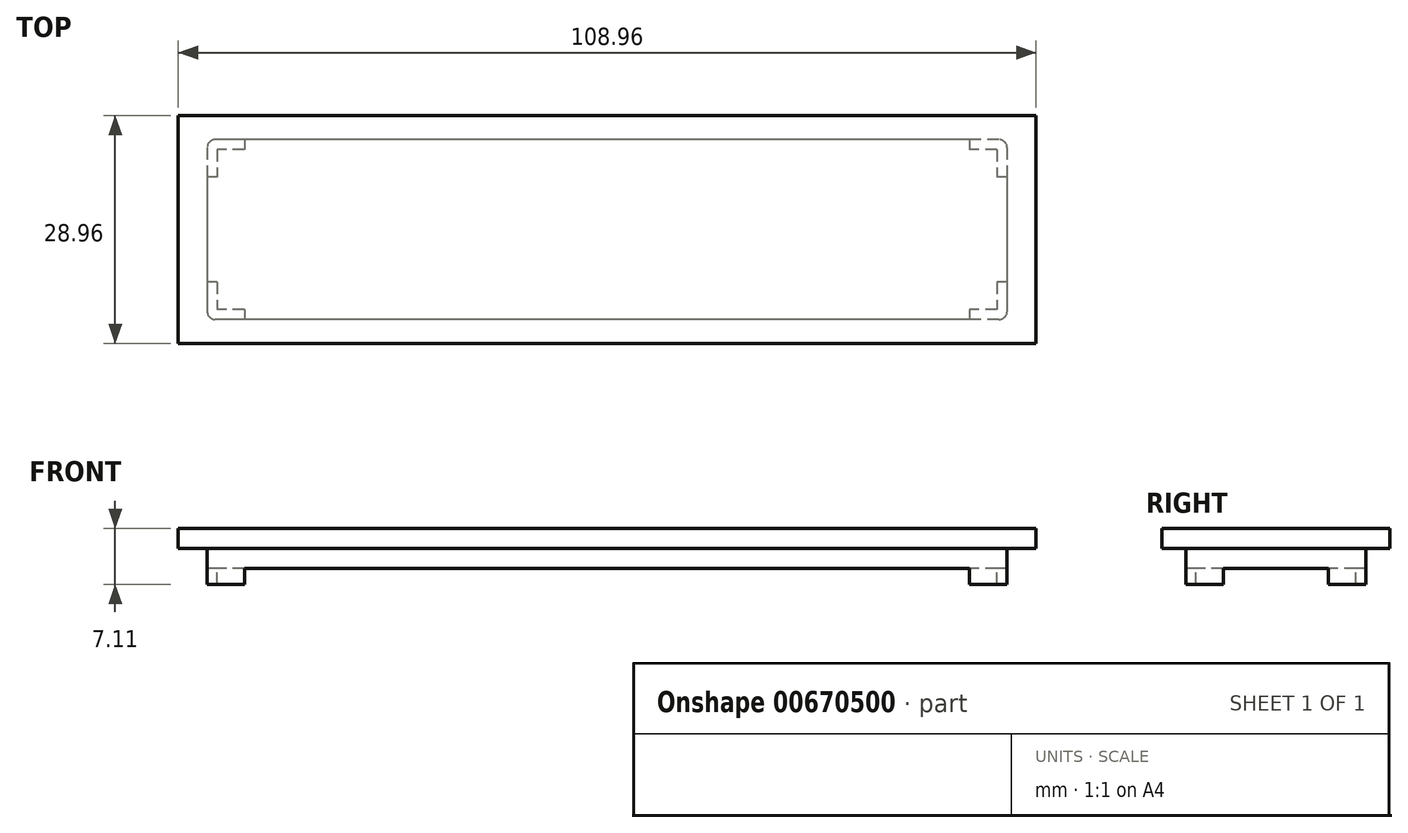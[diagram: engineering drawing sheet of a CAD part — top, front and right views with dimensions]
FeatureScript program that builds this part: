
annotation { "Feature Type Name" : "Feature", "Feature Type Description" : "" }
export const myFeature = defineFeature(function(context is Context, id is Id, definition is map)
    precondition{}
    {
        {
            var Q0;
            Q0=qCreatedBy(makeId("Top.planeOp"),FACE);
            var sketch = newSketch(context, id + "F0", { "sketchPlane" : qUnion([Q0])});
            skLineSegment(sketch, "E0.bottom", {"start": v(50.8, 11.43) * mm, "end": v(-50.8, 11.43) * mm});
            skLineSegment(sketch, "E0.top", {"start": v(50.8, -11.43) * mm, "end": v(-50.8, -11.43) * mm});
            skLineSegment(sketch, "E0.left", {"start": v(50.8, 11.43) * mm, "end": v(50.8, -11.43) * mm});
            skLineSegment(sketch, "E0.right", {"start": v(-50.8, 11.43) * mm, "end": v(-50.8, -11.43) * mm});
            skPoint(sketch, "E0.middle", {"position": v(0, 0) * mm});
            skLineSegment(sketch, "E1.bottom", {"start": v(54.48, 14.48) * mm, "end": v(-54.48, 14.48) * mm});
            skLineSegment(sketch, "E1.top", {"start": v(54.48, -14.48) * mm, "end": v(-54.48, -14.48) * mm});
            skLineSegment(sketch, "E1.left", {"start": v(54.48, 14.48) * mm, "end": v(54.48, -14.48) * mm});
            skLineSegment(sketch, "E1.right", {"start": v(-54.48, 14.48) * mm, "end": v(-54.48, -14.48) * mm});
            skSolve(sketch);
        }
        {
            var Q0;
            Q0=makeQuery(id+"F0.imprint","IMPRINT",FACE,{"disambiguationData":[TD([[makeQuery(id+"F0.imprint","IMPRINT",EDGE,{"derivedFrom":sQuery(id+"F0.wireOp",EDGE,"E0.bottom")}),-1.0]])]});
            var Q1;
            Q1=makeQuery(id+"F0.imprint","IMPRINT",FACE,{"disambiguationData":[TD([[makeQuery(id+"F0.imprint","IMPRINT",EDGE,{"derivedFrom":sQuery(id+"F0.wireOp",EDGE,"E0.bottom")}),1.0]])]});
            extrude(context, id + "F1", {"entities" : qUnion([Q0, Q1]), "depth" : 2.54 * mm, "offsetDistance" : 25.4 * mm});
        }
        {
            var Q0;
            Q0=makeQuery(id+"F0.imprint","IMPRINT",FACE,{"disambiguationData":[TD([[makeQuery(id+"F0.imprint","IMPRINT",EDGE,{"derivedFrom":sQuery(id+"F0.wireOp",EDGE,"E0.bottom")}),1.0]])]});
            extrude(context, id + "F2", {"entities" : qUnion([Q0]), "operationType" : NewBodyOperationType.ADD, "depth" : -2.54 * mm, "offsetDistance" : 25.4 * mm});
        }
        {
            var Q0;
            Q0=makeQuery(id+"F2.opExtrude","CAP_FACE",FACE,{"disambiguationData":[OSD([sQuery(id+"F0.wireOp",EDGE,"E0.bottom"),sQuery(id+"F0.wireOp",EDGE,"E0.top"),sQuery(id+"F0.wireOp",EDGE,"E0.left"),sQuery(id+"F0.wireOp",EDGE,"E0.right")])],"isStart":false});
            var sketch = newSketch(context, id + "F3", { "sketchPlane" : qUnion([Q0])});
            skLineSegment(sketch, "E2.0", {"start": v(50.8, 11.43) * mm, "end": v(46.05, 11.43) * mm});
            skLineSegment(sketch, "E2.1", {"start": v(-50.8, -11.43) * mm, "end": v(-50.8, -6.68) * mm});
            skLineSegment(sketch, "E2.2", {"start": v(50.8, -11.43) * mm, "end": v(46.05, -11.43) * mm});
            skLineSegment(sketch, "E2.3", {"start": v(50.8, -11.43) * mm, "end": v(50.8, -6.68) * mm});
            skLineSegment(sketch, "E3.0", {"start": v(49.53, 10.16) * mm, "end": v(46.05, 10.16) * mm});
            skLineSegment(sketch, "E3.1", {"start": v(49.53, -10.16) * mm, "end": v(49.53, -6.68) * mm});
            skLineSegment(sketch, "E3.2", {"start": v(49.53, -10.16) * mm, "end": v(46.05, -10.16) * mm});
            skLineSegment(sketch, "E3.3", {"start": v(-49.53, -10.16) * mm, "end": v(-49.53, -6.68) * mm});
            skLineSegment(sketch, "E4.0", {"start": v(-46.05, -11.43) * mm, "end": v(-46.05, -10.16) * mm});
            skLineSegment(sketch, "E5.0", {"start": v(46.05, -11.43) * mm, "end": v(46.05, -10.16) * mm});
            skLineSegment(sketch, "E6.0", {"start": v(50.8, 6.68) * mm, "end": v(49.53, 6.68) * mm});
            skLineSegment(sketch, "E7.0", {"start": v(50.8, -6.68) * mm, "end": v(49.53, -6.68) * mm});
            skLineSegment(sketch, "E8.trimOffspring", {"start": v(-46.05, 10.16) * mm, "end": v(-46.05, 11.43) * mm});
            skLineSegment(sketch, "E9.trimOffspring", {"start": v(-49.53, 6.68) * mm, "end": v(-50.8, 6.68) * mm});
            skLineSegment(sketch, "E10.trimOffspring", {"start": v(-49.53, 6.68) * mm, "end": v(-49.53, 10.16) * mm});
            skLineSegment(sketch, "E11.trimOffspring", {"start": v(-46.05, 10.16) * mm, "end": v(-49.53, 10.16) * mm});
            skLineSegment(sketch, "E12.trimOffspring", {"start": v(-49.53, -6.68) * mm, "end": v(-50.8, -6.68) * mm});
            skLineSegment(sketch, "E13.trimOffspring", {"start": v(-46.05, -10.16) * mm, "end": v(-49.53, -10.16) * mm});
            skLineSegment(sketch, "E14.trimOffspring", {"start": v(-50.8, 6.68) * mm, "end": v(-50.8, 11.43) * mm});
            skLineSegment(sketch, "E15.trimOffspring", {"start": v(-46.05, 11.43) * mm, "end": v(-50.8, 11.43) * mm});
            skLineSegment(sketch, "E16.trimOffspring", {"start": v(-46.05, -11.43) * mm, "end": v(-50.8, -11.43) * mm});
            skLineSegment(sketch, "E17.trimOffspring", {"start": v(46.05, 10.16) * mm, "end": v(46.05, 11.43) * mm});
            skLineSegment(sketch, "E18.trimOffspring", {"start": v(49.53, 6.68) * mm, "end": v(49.53, 10.16) * mm});
            skLineSegment(sketch, "E19.trimOffspring", {"start": v(50.8, 6.68) * mm, "end": v(50.8, 11.43) * mm});
            skLineSegment(sketch, "E20.trimOffspring", {"start": v(46.05, -6.68) * mm, "end": v(46.05, 6.68) * mm});
            skSolve(sketch);
        }
        {
            var Q0;
            Q0=makeQuery(id+"F3.imprint","IMPRINT",FACE,{"disambiguationData":[TD([[makeQuery(id+"F3.imprint","IMPRINT",EDGE,{"derivedFrom":sQuery(id+"F3.wireOp",EDGE,"E2.1")}),-1.0]])]});
            var Q1;
            Q1=makeQuery(id+"F3.imprint","IMPRINT",FACE,{"disambiguationData":[TD([[makeQuery(id+"F3.imprint","IMPRINT",EDGE,{"derivedFrom":sQuery(id+"F3.wireOp",EDGE,"E2.0")}),1.0]])]});
            var Q2;
            Q2=makeQuery(id+"F3.imprint","IMPRINT",FACE,{"disambiguationData":[TD([[makeQuery(id+"F3.imprint","IMPRINT",EDGE,{"derivedFrom":sQuery(id+"F3.wireOp",EDGE,"E2.2")}),-1.0]])]});
            var Q3;
            Q3=makeQuery(id+"F3.imprint","IMPRINT",FACE,{"disambiguationData":[TD([[makeQuery(id+"F3.imprint","IMPRINT",EDGE,{"derivedFrom":sQuery(id+"F3.wireOp",EDGE,"E8.trimOffspring")}),1.0]])]});
            extrude(context, id + "F4", {"entities" : qUnion([Q0, Q1, Q2, Q3]), "operationType" : NewBodyOperationType.ADD, "depth" : 2.03 * mm, "offsetDistance" : 25.4 * mm});
        }
        {
            var Q0;
            Q0=makeQuery(id+"F4.boolean.opBoolean","MERGE",EDGE,{"derivedFrom":[makeQuery(id+"F2.opExtrude","SWEPT_EDGE",EDGE,{"disambiguationData":[OSD([sQuery(id+"F0.wireOp",EDGE,"E0.top"),sQuery(id+"F0.wireOp",EDGE,"E0.right")])]}),makeQuery(id+"F4.opExtrude","SWEPT_EDGE",EDGE,{"disambiguationData":[OSD([sQuery(id+"F3.wireOp",EDGE,"E14.trimOffspring"),sQuery(id+"F3.wireOp",EDGE,"E15.trimOffspring")])]})]});
            var Q1;
            Q1=makeQuery(id+"F4.boolean.opBoolean","MERGE",EDGE,{"derivedFrom":[makeQuery(id+"F2.opExtrude","SWEPT_EDGE",EDGE,{"disambiguationData":[OSD([sQuery(id+"F0.wireOp",EDGE,"E0.bottom"),sQuery(id+"F0.wireOp",EDGE,"E0.right")])]}),makeQuery(id+"F4.opExtrude","SWEPT_EDGE",EDGE,{"disambiguationData":[OSD([sQuery(id+"F3.wireOp",EDGE,"E2.1"),sQuery(id+"F3.wireOp",EDGE,"E16.trimOffspring")])]})]});
            var Q2;
            Q2=makeQuery(id+"F4.boolean.opBoolean","MERGE",EDGE,{"derivedFrom":[makeQuery(id+"F2.opExtrude","SWEPT_EDGE",EDGE,{"disambiguationData":[OSD([sQuery(id+"F0.wireOp",EDGE,"E0.bottom"),sQuery(id+"F0.wireOp",EDGE,"E0.left")])]}),makeQuery(id+"F4.opExtrude","SWEPT_EDGE",EDGE,{"disambiguationData":[OSD([sQuery(id+"F3.wireOp",EDGE,"E2.2"),sQuery(id+"F3.wireOp",EDGE,"E2.3")])]})]});
            var Q3;
            Q3=makeQuery(id+"F4.boolean.opBoolean","MERGE",EDGE,{"derivedFrom":[makeQuery(id+"F2.opExtrude","SWEPT_EDGE",EDGE,{"disambiguationData":[OSD([sQuery(id+"F0.wireOp",EDGE,"E0.top"),sQuery(id+"F0.wireOp",EDGE,"E0.left")])]}),makeQuery(id+"F4.opExtrude","SWEPT_EDGE",EDGE,{"disambiguationData":[OSD([sQuery(id+"F3.wireOp",EDGE,"E2.0"),sQuery(id+"F3.wireOp",EDGE,"E19.trimOffspring")])]})]});
            fillet(context, id + "F5", {"entities" : qUnion([Q0, Q1, Q2, Q3]), "radius" : 1.02 * mm, "tangentPropagation" : true, "allowEdgeOverflow" : false});
        }
    });
